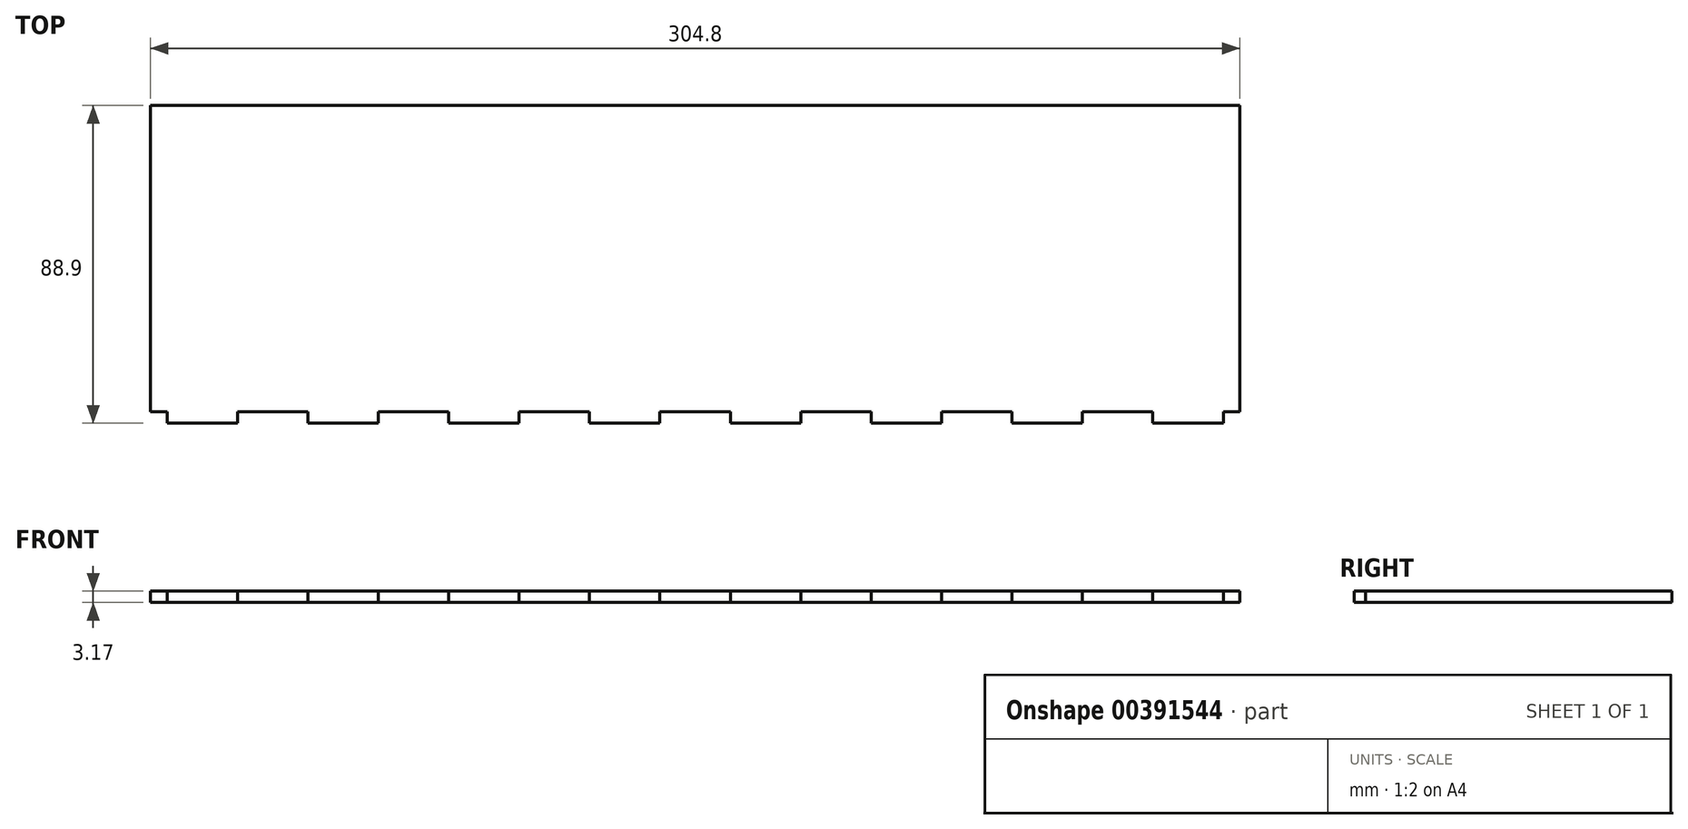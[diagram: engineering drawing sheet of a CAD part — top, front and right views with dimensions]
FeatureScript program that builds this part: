
annotation { "Feature Type Name" : "Feature", "Feature Type Description" : "" }
export const myFeature = defineFeature(function(context is Context, id is Id, definition is map)
    precondition{}
    {
        {
            var Q0;
            Q0=qCreatedBy(makeId("Top.planeOp"),FACE);
            var sketch = newSketch(context, id + "F0", { "sketchPlane" : qUnion([Q0])});
            skLineSegment(sketch, "E0.right", {"start": v(-384.18, -158.75) * mm, "end": v(-384.18, 158.75) * mm, "construction": true});
            skPoint(sketch, "E0.middle", {"position": v(0, 0) * mm});
            skLineSegment(sketch, "E1.bottom", {"start": v(-384.18, 158.75) * mm, "end": v(-364.47, 158.75) * mm});
            skLineSegment(sketch, "E1.left", {"start": v(-384.18, 158.75) * mm, "end": v(-384.18, 142.04) * mm});
            skLineSegment(sketch, "E2.right", {"start": v(-381, 142.04) * mm, "end": v(-381, 125.33) * mm});
            skLineSegment(sketch, "E3", {"start": v(-384.18, 142.04) * mm, "end": v(-381, 142.04) * mm});
            skLineSegment(sketch, "E4", {"start": v(-364.47, 158.75) * mm, "end": v(-364.47, 155.57) * mm});
            skLineSegment(sketch, "E5", {"start": v(-364.47, 155.57) * mm, "end": v(-344.77, 155.57) * mm});
            skLineSegment(sketch, "E6", {"start": v(384.18, 158.75) * mm, "end": v(-384.18, 158.75) * mm, "construction": true});
            skLineSegment(sketch, "E7", {"start": v(-381, 125.33) * mm, "end": v(-384.18, 125.33) * mm});
            skLineSegment(sketch, "E8.1.0.1", {"start": v(-384.18, 108.62) * mm, "end": v(-381, 108.62) * mm});
            skLineSegment(sketch, "E8.1.0.3", {"start": v(-384.17, 125.33) * mm, "end": v(-384.18, 108.62) * mm});
            skLineSegment(sketch, "E8.9.0.1", {"start": v(-384.17, -158.75) * mm, "end": v(-381, -158.75) * mm});
            skLineSegment(sketch, "E8.direction1", {"start": v(-384.18, 125.33) * mm, "end": v(-384.18, 91.9) * mm, "construction": true});
            skLineSegment(sketch, "E9", {"start": v(-344.77, 155.57) * mm, "end": v(-344.77, 158.75) * mm});
            skLineSegment(sketch, "E10.1.0.0", {"start": v(-325.07, 158.75) * mm, "end": v(-325.07, 155.58) * mm});
            skLineSegment(sketch, "E10.1.0.1", {"start": v(-325.07, 155.58) * mm, "end": v(-305.37, 155.58) * mm});
            skLineSegment(sketch, "E10.1.0.2", {"start": v(-305.37, 155.58) * mm, "end": v(-305.37, 158.75) * mm});
            skLineSegment(sketch, "E10.1.0.3", {"start": v(-344.77, 158.75) * mm, "end": v(-325.07, 158.75) * mm});
            skLineSegment(sketch, "E10.2.0.0", {"start": v(-285.67, 158.75) * mm, "end": v(-285.67, 155.58) * mm});
            skLineSegment(sketch, "E10.2.0.1", {"start": v(-285.67, 155.58) * mm, "end": v(-265.97, 155.58) * mm});
            skLineSegment(sketch, "E10.2.0.2", {"start": v(-265.97, 155.58) * mm, "end": v(-265.97, 158.75) * mm});
            skLineSegment(sketch, "E10.2.0.3", {"start": v(-305.37, 158.75) * mm, "end": v(-285.67, 158.75) * mm});
            skLineSegment(sketch, "E10.3.0.0", {"start": v(-246.27, 158.75) * mm, "end": v(-246.27, 155.58) * mm});
            skLineSegment(sketch, "E10.3.0.1", {"start": v(-246.27, 155.58) * mm, "end": v(-226.56, 155.58) * mm});
            skLineSegment(sketch, "E10.3.0.2", {"start": v(-226.56, 155.58) * mm, "end": v(-226.56, 158.75) * mm});
            skLineSegment(sketch, "E10.3.0.3", {"start": v(-265.97, 158.75) * mm, "end": v(-246.27, 158.75) * mm});
            skLineSegment(sketch, "E10.4.0.0", {"start": v(-206.86, 158.75) * mm, "end": v(-206.86, 155.58) * mm});
            skLineSegment(sketch, "E10.4.0.1", {"start": v(-206.86, 155.58) * mm, "end": v(-187.16, 155.58) * mm});
            skLineSegment(sketch, "E10.4.0.2", {"start": v(-187.16, 155.58) * mm, "end": v(-187.16, 158.75) * mm});
            skLineSegment(sketch, "E10.4.0.3", {"start": v(-226.56, 158.75) * mm, "end": v(-206.86, 158.75) * mm});
            skLineSegment(sketch, "E10.5.0.0", {"start": v(-167.46, 158.75) * mm, "end": v(-167.46, 155.58) * mm});
            skLineSegment(sketch, "E10.5.0.1", {"start": v(-167.46, 155.58) * mm, "end": v(-147.76, 155.58) * mm});
            skLineSegment(sketch, "E10.5.0.2", {"start": v(-147.76, 155.58) * mm, "end": v(-147.76, 158.75) * mm});
            skLineSegment(sketch, "E10.5.0.3", {"start": v(-187.16, 158.75) * mm, "end": v(-167.46, 158.75) * mm});
            skLineSegment(sketch, "E10.6.0.0", {"start": v(-128.06, 158.75) * mm, "end": v(-128.06, 155.58) * mm});
            skLineSegment(sketch, "E10.6.0.1", {"start": v(-128.06, 155.58) * mm, "end": v(-108.36, 155.58) * mm});
            skLineSegment(sketch, "E10.6.0.2", {"start": v(-108.36, 155.58) * mm, "end": v(-108.36, 158.75) * mm});
            skLineSegment(sketch, "E10.6.0.3", {"start": v(-147.76, 158.75) * mm, "end": v(-128.06, 158.75) * mm});
            skLineSegment(sketch, "E10.7.0.0", {"start": v(-88.66, 158.75) * mm, "end": v(-88.66, 155.58) * mm});
            skLineSegment(sketch, "E10.7.0.1", {"start": v(-88.66, 155.58) * mm, "end": v(-68.95, 155.58) * mm});
            skLineSegment(sketch, "E10.7.0.2", {"start": v(-68.95, 155.58) * mm, "end": v(-68.95, 158.75) * mm});
            skLineSegment(sketch, "E10.7.0.3", {"start": v(-108.36, 158.75) * mm, "end": v(-88.66, 158.75) * mm});
            skLineSegment(sketch, "E10.8.0.0", {"start": v(-49.25, 158.75) * mm, "end": v(-49.25, 155.58) * mm});
            skLineSegment(sketch, "E10.8.0.1", {"start": v(-49.25, 155.58) * mm, "end": v(-29.55, 155.58) * mm});
            skLineSegment(sketch, "E10.8.0.2", {"start": v(-29.55, 155.58) * mm, "end": v(-29.55, 158.75) * mm});
            skLineSegment(sketch, "E10.8.0.3", {"start": v(-68.95, 158.75) * mm, "end": v(-49.25, 158.75) * mm});
            skLineSegment(sketch, "E10.9.0.0", {"start": v(-9.85, 158.75) * mm, "end": v(-9.85, 155.58) * mm});
            skLineSegment(sketch, "E10.9.0.1", {"start": v(-9.85, 155.58) * mm, "end": v(9.85, 155.58) * mm});
            skLineSegment(sketch, "E10.9.0.2", {"start": v(9.85, 155.58) * mm, "end": v(9.85, 158.75) * mm});
            skLineSegment(sketch, "E10.9.0.3", {"start": v(-29.55, 158.75) * mm, "end": v(-9.85, 158.75) * mm});
            skLineSegment(sketch, "E10.10.0.0", {"start": v(29.55, 158.75) * mm, "end": v(29.55, 155.58) * mm});
            skLineSegment(sketch, "E10.10.0.1", {"start": v(29.55, 155.58) * mm, "end": v(49.25, 155.58) * mm});
            skLineSegment(sketch, "E10.10.0.2", {"start": v(49.25, 155.58) * mm, "end": v(49.25, 158.75) * mm});
            skLineSegment(sketch, "E10.10.0.3", {"start": v(9.85, 158.75) * mm, "end": v(29.55, 158.75) * mm});
            skLineSegment(sketch, "E10.11.0.0", {"start": v(68.95, 158.75) * mm, "end": v(68.95, 155.58) * mm});
            skLineSegment(sketch, "E10.11.0.1", {"start": v(68.95, 155.58) * mm, "end": v(88.66, 155.58) * mm});
            skLineSegment(sketch, "E10.11.0.2", {"start": v(88.66, 155.58) * mm, "end": v(88.66, 158.75) * mm});
            skLineSegment(sketch, "E10.11.0.3", {"start": v(49.25, 158.75) * mm, "end": v(68.95, 158.75) * mm});
            skLineSegment(sketch, "E10.12.0.0", {"start": v(108.36, 158.75) * mm, "end": v(108.36, 155.58) * mm});
            skLineSegment(sketch, "E10.12.0.3", {"start": v(88.66, 158.75) * mm, "end": v(108.36, 158.75) * mm});
            skLineSegment(sketch, "E10.16.0.2", {"start": v(285.67, 155.58) * mm, "end": v(285.67, 158.75) * mm});
            skLineSegment(sketch, "E10.17.0.0", {"start": v(305.37, 158.75) * mm, "end": v(305.37, 155.58) * mm});
            skLineSegment(sketch, "E10.17.0.1", {"start": v(305.37, 155.58) * mm, "end": v(325.07, 155.58) * mm});
            skLineSegment(sketch, "E10.17.0.2", {"start": v(325.07, 155.58) * mm, "end": v(325.07, 158.75) * mm});
            skLineSegment(sketch, "E10.17.0.3", {"start": v(285.67, 158.75) * mm, "end": v(305.37, 158.75) * mm});
            skLineSegment(sketch, "E10.18.0.0", {"start": v(344.77, 158.75) * mm, "end": v(344.77, 155.58) * mm});
            skLineSegment(sketch, "E10.18.0.1", {"start": v(344.77, 155.58) * mm, "end": v(364.47, 155.58) * mm});
            skLineSegment(sketch, "E10.18.0.2", {"start": v(364.47, 155.58) * mm, "end": v(364.47, 158.75) * mm});
            skLineSegment(sketch, "E10.18.0.3", {"start": v(325.07, 158.75) * mm, "end": v(344.77, 158.75) * mm});
            skLineSegment(sketch, "E10.19.0.3", {"start": v(364.47, 158.75) * mm, "end": v(384.18, 158.75) * mm});
            skLineSegment(sketch, "E10.direction1", {"start": v(-384.18, 158.75) * mm, "end": v(-344.77, 158.75) * mm, "construction": true});
            skLineSegment(sketch, "E11.MirrorCS", {"start": v(384.18, -158.75) * mm, "end": v(384.18, -155.58) * mm});
            skLineSegment(sketch, "E12.MirrorCS", {"start": v(-344.77, -155.57) * mm, "end": v(-344.77, -158.75) * mm});
            skLineSegment(sketch, "E13.MirrorCS", {"start": v(108.36, -158.75) * mm, "end": v(108.36, -155.58) * mm});
            skLineSegment(sketch, "E14.MirrorCS", {"start": v(285.67, -155.58) * mm, "end": v(285.67, -158.75) * mm});
            skLineSegment(sketch, "E15.MirrorCS", {"start": v(-285.67, -158.75) * mm, "end": v(-285.67, -155.58) * mm});
            skLineSegment(sketch, "E16.MirrorCS", {"start": v(49.25, -155.58) * mm, "end": v(49.25, -158.75) * mm});
            skLineSegment(sketch, "E17.MirrorCS", {"start": v(-108.36, -155.58) * mm, "end": v(-108.36, -158.75) * mm});
            skLineSegment(sketch, "E18.MirrorCS", {"start": v(-265.97, -155.58) * mm, "end": v(-265.97, -158.75) * mm});
            skLineSegment(sketch, "E19.MirrorCS", {"start": v(-29.55, -155.58) * mm, "end": v(-29.55, -158.75) * mm});
            skLineSegment(sketch, "E20.MirrorCS", {"start": v(364.47, -155.58) * mm, "end": v(364.47, -158.75) * mm});
            skLineSegment(sketch, "E21.MirrorCS", {"start": v(-206.86, -158.75) * mm, "end": v(-206.86, -155.58) * mm});
            skLineSegment(sketch, "E22.MirrorCS", {"start": v(-147.76, -155.58) * mm, "end": v(-147.76, -158.75) * mm});
            skLineSegment(sketch, "E23.MirrorCS", {"start": v(-305.37, -155.58) * mm, "end": v(-305.37, -158.75) * mm});
            skLineSegment(sketch, "E24.MirrorCS", {"start": v(206.86, -155.58) * mm, "end": v(206.86, -158.75) * mm});
            skLineSegment(sketch, "E25.MirrorCS", {"start": v(344.77, -158.75) * mm, "end": v(344.77, -155.58) * mm});
            skLineSegment(sketch, "E26.MirrorCS", {"start": v(128.06, -155.58) * mm, "end": v(128.06, -158.75) * mm});
            skLineSegment(sketch, "E27.MirrorCS", {"start": v(9.85, -155.58) * mm, "end": v(9.85, -158.75) * mm});
            skLineSegment(sketch, "E28.MirrorCS", {"start": v(-364.47, -158.75) * mm, "end": v(-364.47, -155.57) * mm});
            skLineSegment(sketch, "E29.MirrorCS", {"start": v(325.07, -155.58) * mm, "end": v(325.07, -158.75) * mm});
            skLineSegment(sketch, "E30.MirrorCS", {"start": v(167.46, -155.58) * mm, "end": v(167.46, -158.75) * mm});
            skLineSegment(sketch, "E31.MirrorCS", {"start": v(147.76, -158.75) * mm, "end": v(147.76, -155.58) * mm});
            skLineSegment(sketch, "E32.MirrorCS", {"start": v(305.37, -158.75) * mm, "end": v(305.37, -155.58) * mm});
            skLineSegment(sketch, "E33.MirrorCS", {"start": v(-88.66, -158.75) * mm, "end": v(-88.66, -155.58) * mm});
            skLineSegment(sketch, "E34.MirrorCS", {"start": v(29.55, -158.75) * mm, "end": v(29.55, -155.58) * mm});
            skLineSegment(sketch, "E35.MirrorCS", {"start": v(-128.06, -158.75) * mm, "end": v(-128.06, -155.58) * mm});
            skLineSegment(sketch, "E36.MirrorCS", {"start": v(-226.56, -155.58) * mm, "end": v(-226.56, -158.75) * mm});
            skLineSegment(sketch, "E37.MirrorCS", {"start": v(88.66, -155.58) * mm, "end": v(88.66, -158.75) * mm});
            skLineSegment(sketch, "E38.MirrorCS", {"start": v(246.27, -155.58) * mm, "end": v(246.27, -158.75) * mm});
            skLineSegment(sketch, "E39.MirrorCS", {"start": v(-68.95, -155.58) * mm, "end": v(-68.95, -158.75) * mm});
            skLineSegment(sketch, "E40.MirrorCS", {"start": v(265.97, -158.75) * mm, "end": v(265.97, -155.58) * mm});
            skLineSegment(sketch, "E41.MirrorCS", {"start": v(-325.07, -158.75) * mm, "end": v(-325.07, -155.58) * mm});
            skLineSegment(sketch, "E42.MirrorCS", {"start": v(187.16, -158.75) * mm, "end": v(187.16, -155.58) * mm});
            skLineSegment(sketch, "E43.MirrorCS", {"start": v(-187.16, -155.58) * mm, "end": v(-187.16, -158.75) * mm});
            skLineSegment(sketch, "E44.MirrorCS", {"start": v(-167.46, -158.75) * mm, "end": v(-167.46, -155.58) * mm});
            skLineSegment(sketch, "E45.MirrorCS", {"start": v(-9.85, -158.75) * mm, "end": v(-9.85, -155.58) * mm});
            skLineSegment(sketch, "E46.MirrorCS", {"start": v(-246.27, -158.75) * mm, "end": v(-246.27, -155.58) * mm});
            skLineSegment(sketch, "E47.MirrorCS", {"start": v(226.56, -158.75) * mm, "end": v(226.56, -155.58) * mm});
            skLineSegment(sketch, "E48.MirrorCS", {"start": v(68.95, -158.75) * mm, "end": v(68.95, -155.58) * mm});
            skLineSegment(sketch, "E49.MirrorCS", {"start": v(-49.25, -158.75) * mm, "end": v(-49.25, -155.58) * mm});
            skLineSegment(sketch, "E50.MirrorCS", {"start": v(-68.95, -158.75) * mm, "end": v(-49.25, -158.75) * mm});
            skLineSegment(sketch, "E51.MirrorCS", {"start": v(-226.56, -158.75) * mm, "end": v(-206.86, -158.75) * mm});
            skLineSegment(sketch, "E52.MirrorCS", {"start": v(246.27, -158.75) * mm, "end": v(265.97, -158.75) * mm});
            skLineSegment(sketch, "E53.MirrorCS", {"start": v(206.86, -158.75) * mm, "end": v(226.56, -158.75) * mm});
            skLineSegment(sketch, "E54.MirrorCS", {"start": v(49.25, -158.75) * mm, "end": v(68.95, -158.75) * mm});
            skLineSegment(sketch, "E55.MirrorCS", {"start": v(-265.97, -158.75) * mm, "end": v(-246.27, -158.75) * mm});
            skLineSegment(sketch, "E56.MirrorCS", {"start": v(-108.36, -158.75) * mm, "end": v(-88.66, -158.75) * mm});
            skLineSegment(sketch, "E57.MirrorCS", {"start": v(88.66, -158.75) * mm, "end": v(108.36, -158.75) * mm});
            skLineSegment(sketch, "E58.MirrorCS", {"start": v(-344.77, -158.75) * mm, "end": v(-325.07, -158.75) * mm});
            skLineSegment(sketch, "E59.MirrorCS", {"start": v(285.67, -158.75) * mm, "end": v(305.37, -158.75) * mm});
            skLineSegment(sketch, "E60.MirrorCS", {"start": v(128.06, -158.75) * mm, "end": v(147.76, -158.75) * mm});
            skLineSegment(sketch, "E61.MirrorCS", {"start": v(-384.18, -158.75) * mm, "end": v(-364.47, -158.75) * mm});
            skLineSegment(sketch, "E62.MirrorCS", {"start": v(167.46, -158.75) * mm, "end": v(187.16, -158.75) * mm});
            skLineSegment(sketch, "E63.MirrorCS", {"start": v(325.07, -158.75) * mm, "end": v(344.77, -158.75) * mm});
            skLineSegment(sketch, "E64.MirrorCS", {"start": v(364.47, -158.75) * mm, "end": v(384.18, -158.75) * mm});
            skLineSegment(sketch, "E65.MirrorCS", {"start": v(-29.55, -158.75) * mm, "end": v(-9.85, -158.75) * mm});
            skLineSegment(sketch, "E66.MirrorCS", {"start": v(-187.16, -158.75) * mm, "end": v(-167.46, -158.75) * mm});
            skLineSegment(sketch, "E67.MirrorCS", {"start": v(-305.37, -158.75) * mm, "end": v(-285.67, -158.75) * mm});
            skLineSegment(sketch, "E68.MirrorCS", {"start": v(-147.76, -158.75) * mm, "end": v(-128.06, -158.75) * mm});
            skLineSegment(sketch, "E69.MirrorCS", {"start": v(9.85, -158.75) * mm, "end": v(29.55, -158.75) * mm});
            skLineSegment(sketch, "E70.MirrorCS", {"start": v(29.55, -155.58) * mm, "end": v(49.25, -155.58) * mm});
            skLineSegment(sketch, "E71.MirrorCS", {"start": v(226.56, -155.58) * mm, "end": v(246.27, -155.58) * mm});
            skLineSegment(sketch, "E72.MirrorCS", {"start": v(-88.66, -155.58) * mm, "end": v(-68.95, -155.58) * mm});
            skLineSegment(sketch, "E73.MirrorCS", {"start": v(-49.25, -155.58) * mm, "end": v(-29.55, -155.58) * mm});
            skLineSegment(sketch, "E74.MirrorCS", {"start": v(-206.86, -155.58) * mm, "end": v(-187.16, -155.58) * mm});
            skLineSegment(sketch, "E75.MirrorCS", {"start": v(-364.47, -155.57) * mm, "end": v(-344.77, -155.57) * mm});
            skLineSegment(sketch, "E76.MirrorCS", {"start": v(384.18, -158.75) * mm, "end": v(-384.18, -158.75) * mm, "construction": true});
            skLineSegment(sketch, "E77.MirrorCS", {"start": v(-128.06, -155.58) * mm, "end": v(-108.36, -155.58) * mm});
            skLineSegment(sketch, "E78.MirrorCS", {"start": v(-285.67, -155.58) * mm, "end": v(-265.97, -155.58) * mm});
            skLineSegment(sketch, "E79.MirrorCS", {"start": v(344.77, -155.58) * mm, "end": v(364.47, -155.58) * mm});
            skLineSegment(sketch, "E80.MirrorCS", {"start": v(-9.85, -155.58) * mm, "end": v(9.85, -155.58) * mm});
            skLineSegment(sketch, "E81.MirrorCS", {"start": v(-167.46, -155.58) * mm, "end": v(-147.76, -155.58) * mm});
            skLineSegment(sketch, "E82.MirrorCS", {"start": v(-325.07, -155.58) * mm, "end": v(-305.37, -155.58) * mm});
            skLineSegment(sketch, "E83.MirrorCS", {"start": v(305.37, -155.58) * mm, "end": v(325.07, -155.58) * mm});
            skLineSegment(sketch, "E84.MirrorCS", {"start": v(147.76, -155.58) * mm, "end": v(167.46, -155.58) * mm});
            skLineSegment(sketch, "E85.MirrorCS", {"start": v(265.97, -155.58) * mm, "end": v(285.67, -155.58) * mm});
            skLineSegment(sketch, "E86.MirrorCS", {"start": v(-246.27, -155.58) * mm, "end": v(-226.56, -155.58) * mm});
            skLineSegment(sketch, "E87.MirrorCS", {"start": v(68.95, -155.58) * mm, "end": v(88.66, -155.58) * mm});
            skLineSegment(sketch, "E88.MirrorCS", {"start": v(187.16, -155.58) * mm, "end": v(206.86, -155.58) * mm});
            skLineSegment(sketch, "E89.MirrorCS", {"start": v(-384.18, -158.75) * mm, "end": v(-344.77, -158.75) * mm, "construction": true});
            skLineSegment(sketch, "E90.MirrorCS", {"start": v(108.36, -155.58) * mm, "end": v(128.06, -155.58) * mm});
            skLineSegment(sketch, "E91.MirrorCS", {"start": v(384.17, -158.75) * mm, "end": v(381, -158.75) * mm});
            skLineSegment(sketch, "E92.MirrorCS", {"start": v(384.18, -158.75) * mm, "end": v(384.18, 158.75) * mm, "construction": true});
            skLineSegment(sketch, "E93", {"start": v(104.78, 110.81) * mm, "end": v(104.78, 136.48) * mm, "construction": true});
            skLineSegment(sketch, "E94", {"start": v(168.28, 138.21) * mm, "end": v(168.28, 115.73) * mm, "construction": true});
            skLineSegment(sketch, "E95", {"start": v(108.36, 155.58) * mm, "end": v(111.13, 155.58) * mm});
            skLineSegment(sketch, "E96", {"start": v(285.67, 155.58) * mm, "end": v(268.6, 155.58) * mm});
            skLineSegment(sketch, "E97.MirrorCS", {"start": v(167.46, 155.58) * mm, "end": v(167.46, 158.75) * mm});
            skLineSegment(sketch, "E98.MirrorCS", {"start": v(147.76, 158.75) * mm, "end": v(147.76, 155.58) * mm});
            skLineSegment(sketch, "E99.MirrorCS", {"start": v(128.06, 155.58) * mm, "end": v(128.06, 158.75) * mm});
            skLineSegment(sketch, "E100.MirrorCS", {"start": v(265.97, 158.75) * mm, "end": v(265.97, 155.58) * mm});
            skLineSegment(sketch, "E101.MirrorCS", {"start": v(246.27, 155.58) * mm, "end": v(246.27, 158.75) * mm});
            skLineSegment(sketch, "E102.MirrorCS", {"start": v(226.56, 158.75) * mm, "end": v(226.56, 155.58) * mm});
            skLineSegment(sketch, "E103.MirrorCS", {"start": v(187.16, 158.75) * mm, "end": v(187.16, 155.58) * mm});
            skLineSegment(sketch, "E104.MirrorCS", {"start": v(206.86, 155.58) * mm, "end": v(206.86, 158.75) * mm});
            skLineSegment(sketch, "E105.MirrorCS", {"start": v(265.97, 155.58) * mm, "end": v(285.67, 155.58) * mm});
            skLineSegment(sketch, "E106.MirrorCS", {"start": v(206.86, 158.75) * mm, "end": v(226.56, 158.75) * mm});
            skLineSegment(sketch, "E107.MirrorCS", {"start": v(147.76, 155.58) * mm, "end": v(167.46, 155.58) * mm});
            skLineSegment(sketch, "E108.MirrorCS", {"start": v(246.27, 158.75) * mm, "end": v(265.97, 158.75) * mm});
            skLineSegment(sketch, "E109.MirrorCS", {"start": v(167.46, 158.75) * mm, "end": v(187.16, 158.75) * mm});
            skLineSegment(sketch, "E110.MirrorCS", {"start": v(128.06, 158.75) * mm, "end": v(147.76, 158.75) * mm});
            skLineSegment(sketch, "E111.MirrorCS", {"start": v(108.36, 155.58) * mm, "end": v(128.06, 155.58) * mm});
            skLineSegment(sketch, "E112.MirrorCS", {"start": v(187.16, 155.58) * mm, "end": v(206.86, 155.58) * mm});
            skLineSegment(sketch, "E113.MirrorCS", {"start": v(226.56, 155.58) * mm, "end": v(246.27, 155.58) * mm});
            skLineSegment(sketch, "E114", {"start": v(168.28, 138.21) * mm, "end": v(168.28, 188.5) * mm, "construction": true});
            skLineSegment(sketch, "E115.bottom", {"start": v(104.78, 110.81) * mm, "end": v(168.28, 110.81) * mm});
            skLineSegment(sketch, "E115.top", {"start": v(104.78, 188.5) * mm, "end": v(168.28, 188.5) * mm});
            skLineSegment(sketch, "E115.left", {"start": v(104.78, 110.81) * mm, "end": v(104.77, 188.5) * mm});
            skLineSegment(sketch, "E115.right", {"start": v(168.28, 110.81) * mm, "end": v(168.28, 188.5) * mm});
            skLineSegment(sketch, "E116.1.0.1", {"start": v(-381, 108.62) * mm, "end": v(-381, 91.9) * mm});
            skLineSegment(sketch, "E116.1.0.3", {"start": v(-381, 91.9) * mm, "end": v(-384.18, 91.9) * mm});
            skLineSegment(sketch, "E116.2.0.0", {"start": v(-384.17, 91.9) * mm, "end": v(-384.17, 75.2) * mm});
            skLineSegment(sketch, "E116.2.0.1", {"start": v(-381, 75.2) * mm, "end": v(-381, 58.49) * mm});
            skLineSegment(sketch, "E116.2.0.2", {"start": v(-384.18, 75.2) * mm, "end": v(-381, 75.2) * mm});
            skLineSegment(sketch, "E116.2.0.3", {"start": v(-381, 58.49) * mm, "end": v(-384.17, 58.49) * mm});
            skLineSegment(sketch, "E116.3.0.0", {"start": v(-384.17, 58.49) * mm, "end": v(-384.17, 41.78) * mm});
            skLineSegment(sketch, "E116.3.0.1", {"start": v(-381, 41.78) * mm, "end": v(-381, 25.07) * mm});
            skLineSegment(sketch, "E116.3.0.2", {"start": v(-384.17, 41.78) * mm, "end": v(-381, 41.78) * mm});
            skLineSegment(sketch, "E116.3.0.3", {"start": v(-381, 25.07) * mm, "end": v(-384.17, 25.07) * mm});
            skLineSegment(sketch, "E116.4.0.0", {"start": v(-384.17, 25.07) * mm, "end": v(-384.17, 8.36) * mm});
            skLineSegment(sketch, "E116.4.0.1", {"start": v(-381, 8.36) * mm, "end": v(-381, -8.36) * mm});
            skLineSegment(sketch, "E116.4.0.2", {"start": v(-384.17, 8.36) * mm, "end": v(-381, 8.36) * mm});
            skLineSegment(sketch, "E116.4.0.3", {"start": v(-381, -8.36) * mm, "end": v(-384.17, -8.36) * mm});
            skLineSegment(sketch, "E116.5.0.0", {"start": v(-384.17, -8.36) * mm, "end": v(-384.17, -25.07) * mm});
            skLineSegment(sketch, "E116.5.0.1", {"start": v(-381, -25.07) * mm, "end": v(-381, -41.78) * mm});
            skLineSegment(sketch, "E116.5.0.2", {"start": v(-384.17, -25.07) * mm, "end": v(-381, -25.07) * mm});
            skLineSegment(sketch, "E116.5.0.3", {"start": v(-381, -41.78) * mm, "end": v(-384.17, -41.78) * mm});
            skLineSegment(sketch, "E116.6.0.0", {"start": v(-384.17, -41.78) * mm, "end": v(-384.17, -58.49) * mm});
            skLineSegment(sketch, "E116.6.0.1", {"start": v(-381, -58.49) * mm, "end": v(-381, -75.2) * mm});
            skLineSegment(sketch, "E116.6.0.2", {"start": v(-384.17, -58.49) * mm, "end": v(-381, -58.49) * mm});
            skLineSegment(sketch, "E116.6.0.3", {"start": v(-381, -75.2) * mm, "end": v(-384.17, -75.2) * mm});
            skLineSegment(sketch, "E116.7.0.0", {"start": v(-384.17, -75.2) * mm, "end": v(-384.17, -91.9) * mm});
            skLineSegment(sketch, "E116.7.0.1", {"start": v(-381, -91.9) * mm, "end": v(-381, -108.62) * mm});
            skLineSegment(sketch, "E116.7.0.2", {"start": v(-384.17, -91.9) * mm, "end": v(-381, -91.9) * mm});
            skLineSegment(sketch, "E116.7.0.3", {"start": v(-381, -108.62) * mm, "end": v(-384.17, -108.62) * mm});
            skLineSegment(sketch, "E116.8.0.0", {"start": v(-384.17, -108.62) * mm, "end": v(-384.17, -125.33) * mm});
            skLineSegment(sketch, "E116.8.0.1", {"start": v(-381, -125.33) * mm, "end": v(-381, -142.04) * mm});
            skLineSegment(sketch, "E116.8.0.2", {"start": v(-384.17, -125.33) * mm, "end": v(-381, -125.33) * mm});
            skLineSegment(sketch, "E116.8.0.3", {"start": v(-381, -142.04) * mm, "end": v(-384.17, -142.04) * mm});
            skLineSegment(sketch, "E116.9.0.0", {"start": v(-384.17, -142.04) * mm, "end": v(-384.17, -158.75) * mm});
            skLineSegment(sketch, "E117", {"start": v(-384.18, 125.33) * mm, "end": v(-384.18, 108.62) * mm});
            skLineSegment(sketch, "E118", {"start": v(-384.18, 91.9) * mm, "end": v(-384.18, 75.2) * mm});
            skLineSegment(sketch, "E119.MirrorCS", {"start": v(384.18, 108.62) * mm, "end": v(381, 108.62) * mm});
            skLineSegment(sketch, "E120.MirrorCS", {"start": v(384.17, 125.33) * mm, "end": v(384.18, 108.62) * mm});
            skLineSegment(sketch, "E121.MirrorCS", {"start": v(384.18, 125.33) * mm, "end": v(384.18, 108.62) * mm});
            skLineSegment(sketch, "E122.MirrorCS", {"start": v(381, 91.9) * mm, "end": v(384.18, 91.9) * mm});
            skLineSegment(sketch, "E123.MirrorCS", {"start": v(381, 125.33) * mm, "end": v(384.18, 125.33) * mm});
            skLineSegment(sketch, "E124.MirrorCS", {"start": v(384.17, -142.04) * mm, "end": v(384.17, -158.75) * mm});
            skLineSegment(sketch, "E125.MirrorCS", {"start": v(381, 58.49) * mm, "end": v(384.17, 58.49) * mm});
            skLineSegment(sketch, "E126.MirrorCS", {"start": v(381, -142.04) * mm, "end": v(384.17, -142.04) * mm});
            skLineSegment(sketch, "E127.MirrorCS", {"start": v(384.18, 91.9) * mm, "end": v(384.18, 75.2) * mm});
            skLineSegment(sketch, "E128.MirrorCS", {"start": v(381, -41.78) * mm, "end": v(384.17, -41.78) * mm});
            skLineSegment(sketch, "E129.MirrorCS", {"start": v(381, -8.36) * mm, "end": v(384.17, -8.36) * mm});
            skLineSegment(sketch, "E130.MirrorCS", {"start": v(381, 25.07) * mm, "end": v(384.17, 25.07) * mm});
            skLineSegment(sketch, "E131.MirrorCS", {"start": v(381, -108.62) * mm, "end": v(384.17, -108.62) * mm});
            skLineSegment(sketch, "E132.MirrorCS", {"start": v(381, -75.2) * mm, "end": v(384.17, -75.2) * mm});
            skLineSegment(sketch, "E133.MirrorCS", {"start": v(384.18, 75.2) * mm, "end": v(381, 75.2) * mm});
            skLineSegment(sketch, "E134.MirrorCS", {"start": v(384.17, 91.9) * mm, "end": v(384.17, 75.2) * mm});
            skLineSegment(sketch, "E135.MirrorCS", {"start": v(384.18, 142.04) * mm, "end": v(381, 142.04) * mm});
            skLineSegment(sketch, "E136.MirrorCS", {"start": v(384.17, 58.49) * mm, "end": v(384.17, 41.78) * mm});
            skLineSegment(sketch, "E137.MirrorCS", {"start": v(384.17, -58.49) * mm, "end": v(381, -58.49) * mm});
            skLineSegment(sketch, "E138.MirrorCS", {"start": v(381, -58.49) * mm, "end": v(381, -75.2) * mm});
            skLineSegment(sketch, "E139.MirrorCS", {"start": v(384.17, -25.07) * mm, "end": v(381, -25.07) * mm});
            skLineSegment(sketch, "E140.MirrorCS", {"start": v(381, -25.07) * mm, "end": v(381, -41.78) * mm});
            skLineSegment(sketch, "E141.MirrorCS", {"start": v(384.17, 8.36) * mm, "end": v(381, 8.36) * mm});
            skLineSegment(sketch, "E142.MirrorCS", {"start": v(384.17, -125.33) * mm, "end": v(381, -125.33) * mm});
            skLineSegment(sketch, "E143.MirrorCS", {"start": v(384.17, -108.62) * mm, "end": v(384.17, -125.33) * mm});
            skLineSegment(sketch, "E144.MirrorCS", {"start": v(384.17, 41.78) * mm, "end": v(381, 41.78) * mm});
            skLineSegment(sketch, "E145.MirrorCS", {"start": v(384.17, -91.9) * mm, "end": v(381, -91.9) * mm});
            skLineSegment(sketch, "E146.MirrorCS", {"start": v(381, 8.36) * mm, "end": v(381, -8.36) * mm});
            skLineSegment(sketch, "E147.MirrorCS", {"start": v(384.18, 158.75) * mm, "end": v(384.18, 142.04) * mm});
            skLineSegment(sketch, "E148.MirrorCS", {"start": v(384.17, -41.78) * mm, "end": v(384.17, -58.49) * mm});
            skLineSegment(sketch, "E149.MirrorCS", {"start": v(384.17, 25.07) * mm, "end": v(384.17, 8.36) * mm});
            skLineSegment(sketch, "E150.MirrorCS", {"start": v(384.17, -8.36) * mm, "end": v(384.17, -25.07) * mm});
            skLineSegment(sketch, "E151.MirrorCS", {"start": v(384.17, -75.2) * mm, "end": v(384.17, -91.9) * mm});
            skLineSegment(sketch, "E152.MirrorCS", {"start": v(384.18, 125.33) * mm, "end": v(384.18, 91.9) * mm, "construction": true});
            skLineSegment(sketch, "E153.MirrorCS", {"start": v(381, 142.04) * mm, "end": v(381, 125.33) * mm});
            skLineSegment(sketch, "E154.MirrorCS", {"start": v(381, 41.78) * mm, "end": v(381, 25.07) * mm});
            skLineSegment(sketch, "E155.MirrorCS", {"start": v(381, -91.9) * mm, "end": v(381, -108.62) * mm});
            skLineSegment(sketch, "E156.MirrorCS", {"start": v(381, 75.2) * mm, "end": v(381, 58.49) * mm});
            skLineSegment(sketch, "E157.MirrorCS", {"start": v(381, 108.62) * mm, "end": v(381, 91.9) * mm});
            skLineSegment(sketch, "E158.MirrorCS", {"start": v(381, -125.33) * mm, "end": v(381, -142.04) * mm});
            skLineSegment(sketch, "E159.bottom", {"start": v(-152.4, -233.88) * mm, "end": v(152.4, -233.88) * mm});
            skLineSegment(sketch, "E159.top", {"start": v(-152.4, -69.85) * mm, "end": v(152.4, -69.85) * mm});
            skLineSegment(sketch, "E159.left", {"start": v(-152.4, -233.88) * mm, "end": v(-152.4, -69.85) * mm});
            skLineSegment(sketch, "E159.right", {"start": v(152.4, -233.88) * mm, "end": v(152.4, -69.85) * mm});
            skSolve(sketch);
        }
        {
            var Q0;
            Q0=makeQuery(id+"F0.imprint","IMPRINT",FACE,{"disambiguationData":[TD([[makeQuery(id+"F0.imprint","IMPRINT",EDGE,{"derivedFrom":sQuery(id+"F0.wireOp",EDGE,"E13.MirrorCS")}),1.0]])]});
            extrude(context, id + "F1", {"entities" : qUnion([Q0]), "depth" : 3.17 * mm});
        }
    });
